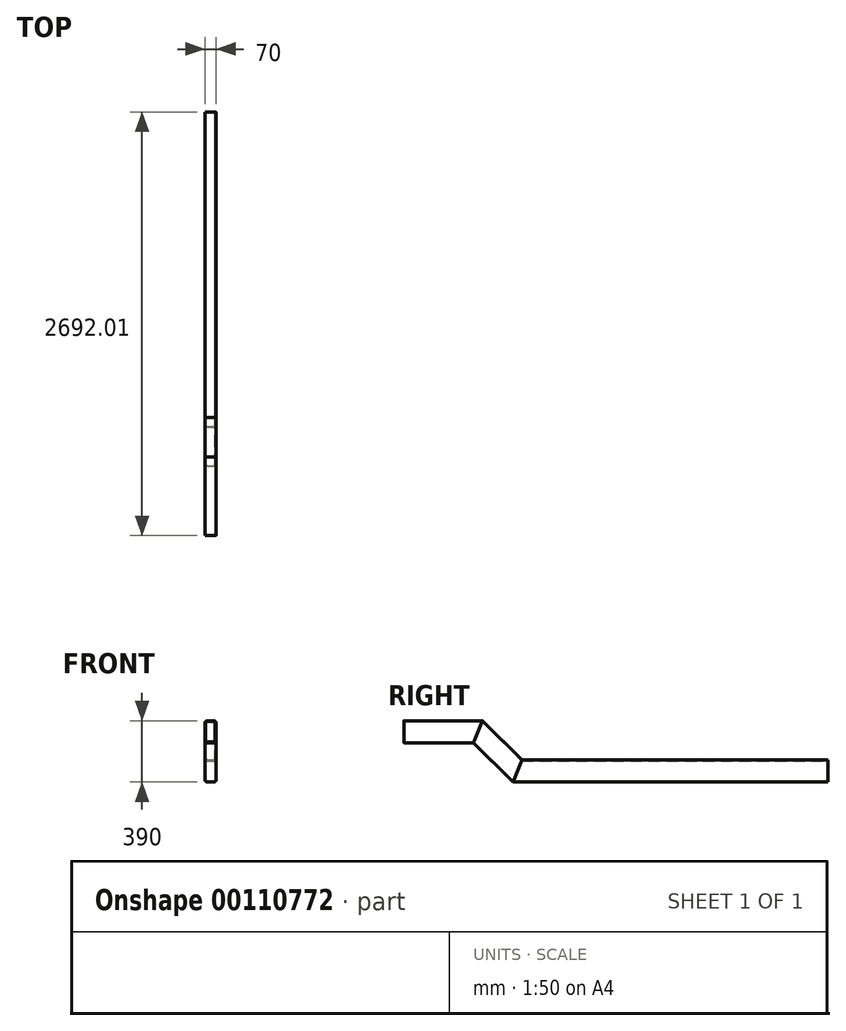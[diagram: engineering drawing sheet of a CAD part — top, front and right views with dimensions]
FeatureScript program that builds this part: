
annotation { "Feature Type Name" : "Feature", "Feature Type Description" : "" }
export const myFeature = defineFeature(function(context is Context, id is Id, definition is map)
    precondition{}
    {
        {
            var Q0;
            Q0=qCreatedBy(makeId("Front.planeOp"),FACE);
            var sketch = newSketch(context, id + "F0", { "sketchPlane" : qUnion([Q0])});
            skLineSegment(sketch, "E0.bottom", {"start": v(-35, 70) * mm, "end": v(35, 70) * mm});
            skLineSegment(sketch, "E0.top", {"start": v(-35, -70) * mm, "end": v(35, -70) * mm});
            skLineSegment(sketch, "E0.left", {"start": v(-35, 70) * mm, "end": v(-35, -70) * mm});
            skLineSegment(sketch, "E0.right", {"start": v(35, 70) * mm, "end": v(35, -70) * mm});
            skLineSegment(sketch, "E1", {"start": v(0, 70) * mm, "end": v(0, -70) * mm, "construction": true});
            skLineSegment(sketch, "E2", {"start": v(-35, 0) * mm, "end": v(35, 0) * mm, "construction": true});
            skSolve(sketch);
        }
        {
            var Q0;
            Q0=makeQuery(id+"F0.imprint","IMPRINT",FACE,{"disambiguationData":[TD([[makeQuery(id+"F0.imprint","IMPRINT",EDGE,{"derivedFrom":sQuery(id+"F0.wireOp",EDGE,"E0.bottom")}),-1.0]])]});
            extrude(context, id + "F1", {"entities" : qUnion([Q0]), "endBound" : BoundingType.SYMMETRIC, "depth" : 2000 * mm});
        }
        {
            var Q0;
            Q0=makeQuery(id+"F1.opExtrude","SWEPT_FACE",FACE,{"disambiguationData":[OSD([sQuery(id+"F0.wireOp",EDGE,"E0.right")])]});
            var sketch = newSketch(context, id + "F2", { "sketchPlane" : qUnion([Q0])});
            skLineSegment(sketch, "E3", {"start": v(-1000, -70) * mm, "end": v(-1250, 180) * mm});
            skLineSegment(sketch, "E4.0", {"start": v(-942.01, 70) * mm, "end": v(-1151, 279) * mm});
            skLineSegment(sketch, "E5", {"start": v(-1250, 180) * mm, "end": v(-1151, 279) * mm, "construction": true});
            skLineSegment(sketch, "E6", {"start": v(-942.01, 70) * mm, "end": v(-1000, -70) * mm});
            skPoint(sketch, "E7.orphan", {"position": v(-950.5, 49.5) * mm});
            skPoint(sketch, "E8.end.orphan", {"position": v(-901, 29) * mm});
            skPoint(sketch, "E9.start.orphan", {"position": v(-1000, 70) * mm});
            skLineSegment(sketch, "E10", {"start": v(-1250, 180) * mm, "end": v(-1192.01, 320) * mm});
            skLineSegment(sketch, "E11", {"start": v(-1151, 279) * mm, "end": v(-1192.01, 320) * mm});
            skSolve(sketch);
        }
        {
            var Q0;
            {var subQ0=sQuery(id+"F2.wireOp",EDGE,"E6");Q0=makeQuery(id+"F2.imprint","IMPRINT",FACE,{"disambiguationData":[TD([[makeQuery(id+"F2.imprint","IMPRINT",EDGE,{"derivedFrom":subQ0}),-1.0]])]});}
            extrude(context, id + "F3", {"entities" : qUnion([Q0]), "operationType" : NewBodyOperationType.REMOVE, "oppositeDirection" : true, "depth" : 70 * mm});
        }
        {
            var Q0;
            Q0=makeQuery(id+"F2.imprint","IMPRINT",FACE,{"disambiguationData":[TD([[makeQuery(id+"F2.imprint","IMPRINT",EDGE,{"derivedFrom":sQuery(id+"F2.wireOp",EDGE,"E3")}),-1.0]])]});
            var Q1;
            {var subQ0=sQuery(id+"F2.wireOp",EDGE,"E6");Q1=makeQuery(id+"F2.imprint","IMPRINT",FACE,{"disambiguationData":[TD([[makeQuery(id+"F2.imprint","IMPRINT",EDGE,{"derivedFrom":subQ0}),-1.0]])]});}
            var Q2;
            Q2=sQuery(id+"F2.wireOp",EDGE,"E5");
            extrude(context, id + "F4", {"entities" : qUnion([Q0, Q1]), "surfaceEntities" : qUnion([Q2]), "oppositeDirection" : true, "depth" : 70 * mm});
        }
        {
            var Q0;
            Q0=makeQuery(id+"F1.opExtrude","SWEPT_EDGE",EDGE,{"disambiguationData":[OSD([sQuery(id+"F0.wireOp",EDGE,"E0.bottom"),sQuery(id+"F0.wireOp",EDGE,"E0.right")])]});
            var Q1;
            Q1=makeQuery(id+"F1.opExtrude","SWEPT_EDGE",EDGE,{"disambiguationData":[OSD([sQuery(id+"F0.wireOp",EDGE,"E0.bottom"),sQuery(id+"F0.wireOp",EDGE,"E0.left")])]});
            var Q2;
            Q2=makeQuery(id+"F1.opExtrude","SWEPT_EDGE",EDGE,{"disambiguationData":[OSD([sQuery(id+"F0.wireOp",EDGE,"E0.top"),sQuery(id+"F0.wireOp",EDGE,"E0.right")])]});
            var Q3;
            Q3=makeQuery(id+"F1.opExtrude","SWEPT_EDGE",EDGE,{"disambiguationData":[OSD([sQuery(id+"F0.wireOp",EDGE,"E0.top"),sQuery(id+"F0.wireOp",EDGE,"E0.left")])]});
            fillet(context, id + "F5", {"entities" : qUnion([Q0, Q1, Q2, Q3]), "radius" : 15 * mm, "tangentPropagation" : true, "allowEdgeOverflow" : false});
        }
        {
            var Q0;
            Q0=makeQuery(id+"F3.boolean.opBoolean","COPY",FACE,{"derivedFrom":makeQuery(id+"F3.opExtrude","SWEPT_FACE",FACE,{"disambiguationData":[OSD([sQuery(id+"F2.wireOp",EDGE,"E6")])]})});
            var Q1;
            Q1=makeQuery(id+"F1.opExtrude","CAP_FACE",FACE,{"disambiguationData":[OSD([sQuery(id+"F0.wireOp",EDGE,"E0.bottom"),sQuery(id+"F0.wireOp",EDGE,"E0.top"),sQuery(id+"F0.wireOp",EDGE,"E0.left"),sQuery(id+"F0.wireOp",EDGE,"E0.right")])],"isStart":true});
            shell(context, id + "F6", {"entities" : qUnion([Q0, Q1]), "thickness" : 5 * mm});
        }
        {
            var Q0;
            Q0=makeQuery(id+"F4.opExtrude","CAP_FACE",FACE,{"disambiguationData":[OSD([sQuery(id+"F2.wireOp",EDGE,"E3"),sQuery(id+"F2.wireOp",EDGE,"E4.0"),sQuery(id+"F2.wireOp",EDGE,"E6"),sQuery(id+"F2.wireOp",EDGE,"E10"),sQuery(id+"F2.wireOp",EDGE,"E11")])],"isStart":false});
            var sketch = newSketch(context, id + "F7", { "sketchPlane" : qUnion([Q0])});
            skLineSegment(sketch, "E12", {"start": v(1192.01, 320) * mm, "end": v(1692.01, 320) * mm});
            skLineSegment(sketch, "E13", {"start": v(1692.01, 320) * mm, "end": v(1692.01, 180) * mm});
            skLineSegment(sketch, "E14", {"start": v(1250, 180) * mm, "end": v(1692.01, 180) * mm});
            skLineSegment(sketch, "E15", {"start": v(1192.01, 320) * mm, "end": v(1250, 180) * mm});
            skSolve(sketch);
        }
        {
            var Q0;
            Q0=makeQuery(id+"F7.imprint","IMPRINT",FACE,{"disambiguationData":[TD([[makeQuery(id+"F7.imprint","IMPRINT",EDGE,{"derivedFrom":sQuery(id+"F7.wireOp",EDGE,"E12")}),-1.0]])]});
            extrude(context, id + "F8", {"entities" : qUnion([Q0]), "oppositeDirection" : true, "depth" : 70 * mm});
        }
        {
            var Q0;
            Q0=makeQuery(id+"F4.opExtrude","CAP_EDGE",EDGE,{"disambiguationData":[OSD([sQuery(id+"F2.wireOp",EDGE,"E4.0"),sQuery(id+"F2.wireOp",EDGE,"E11")])],"isStart":true});
            var Q1;
            Q1=makeQuery(id+"F4.opExtrude","CAP_EDGE",EDGE,{"disambiguationData":[OSD([sQuery(id+"F2.wireOp",EDGE,"E4.0"),sQuery(id+"F2.wireOp",EDGE,"E11")])],"isStart":false});
            var Q2;
            Q2=makeQuery(id+"F4.opExtrude","CAP_EDGE",EDGE,{"disambiguationData":[OSD([sQuery(id+"F2.wireOp",EDGE,"E3")])],"isStart":true});
            var Q3;
            Q3=makeQuery(id+"F4.opExtrude","CAP_EDGE",EDGE,{"disambiguationData":[OSD([sQuery(id+"F2.wireOp",EDGE,"E3")])],"isStart":false});
            var Q4;
            Q4=makeQuery(id+"F8.opExtrude","CAP_EDGE",EDGE,{"disambiguationData":[OSD([sQuery(id+"F7.wireOp",EDGE,"E14")])],"isStart":false});
            var Q5;
            Q5=makeQuery(id+"F8.opExtrude","CAP_EDGE",EDGE,{"disambiguationData":[OSD([sQuery(id+"F7.wireOp",EDGE,"E14")])],"isStart":true});
            var Q6;
            Q6=makeQuery(id+"F8.opExtrude","CAP_EDGE",EDGE,{"disambiguationData":[OSD([sQuery(id+"F7.wireOp",EDGE,"E12")])],"isStart":true});
            var Q7;
            Q7=makeQuery(id+"F8.opExtrude","CAP_EDGE",EDGE,{"disambiguationData":[OSD([sQuery(id+"F7.wireOp",EDGE,"E12")])],"isStart":false});
            fillet(context, id + "F9", {"entities" : qUnion([Q0, Q1, Q2, Q3, Q4, Q5, Q6, Q7]), "radius" : 15 * mm, "tangentPropagation" : true, "allowEdgeOverflow" : false});
        }
        {
            var Q0;
            Q0=makeQuery(id+"F4.opExtrude","SWEPT_FACE",FACE,{"disambiguationData":[OSD([sQuery(id+"F2.wireOp",EDGE,"E6")])]});
            var Q1;
            Q1=makeQuery(id+"F4.opExtrude","SWEPT_FACE",FACE,{"disambiguationData":[OSD([sQuery(id+"F2.wireOp",EDGE,"E10")])]});
            shell(context, id + "F10", {"entities" : qUnion([Q0, Q1]), "thickness" : 5 * mm});
        }
        {
            var Q0;
            Q0=makeQuery(id+"F8.opExtrude","SWEPT_FACE",FACE,{"disambiguationData":[OSD([sQuery(id+"F7.wireOp",EDGE,"E15")])]});
            var Q1;
            Q1=makeQuery(id+"F8.opExtrude","SWEPT_FACE",FACE,{"disambiguationData":[OSD([sQuery(id+"F7.wireOp",EDGE,"E13")])]});
            shell(context, id + "F11", {"entities" : qUnion([Q0, Q1]), "thickness" : 5 * mm});
        }
    });
